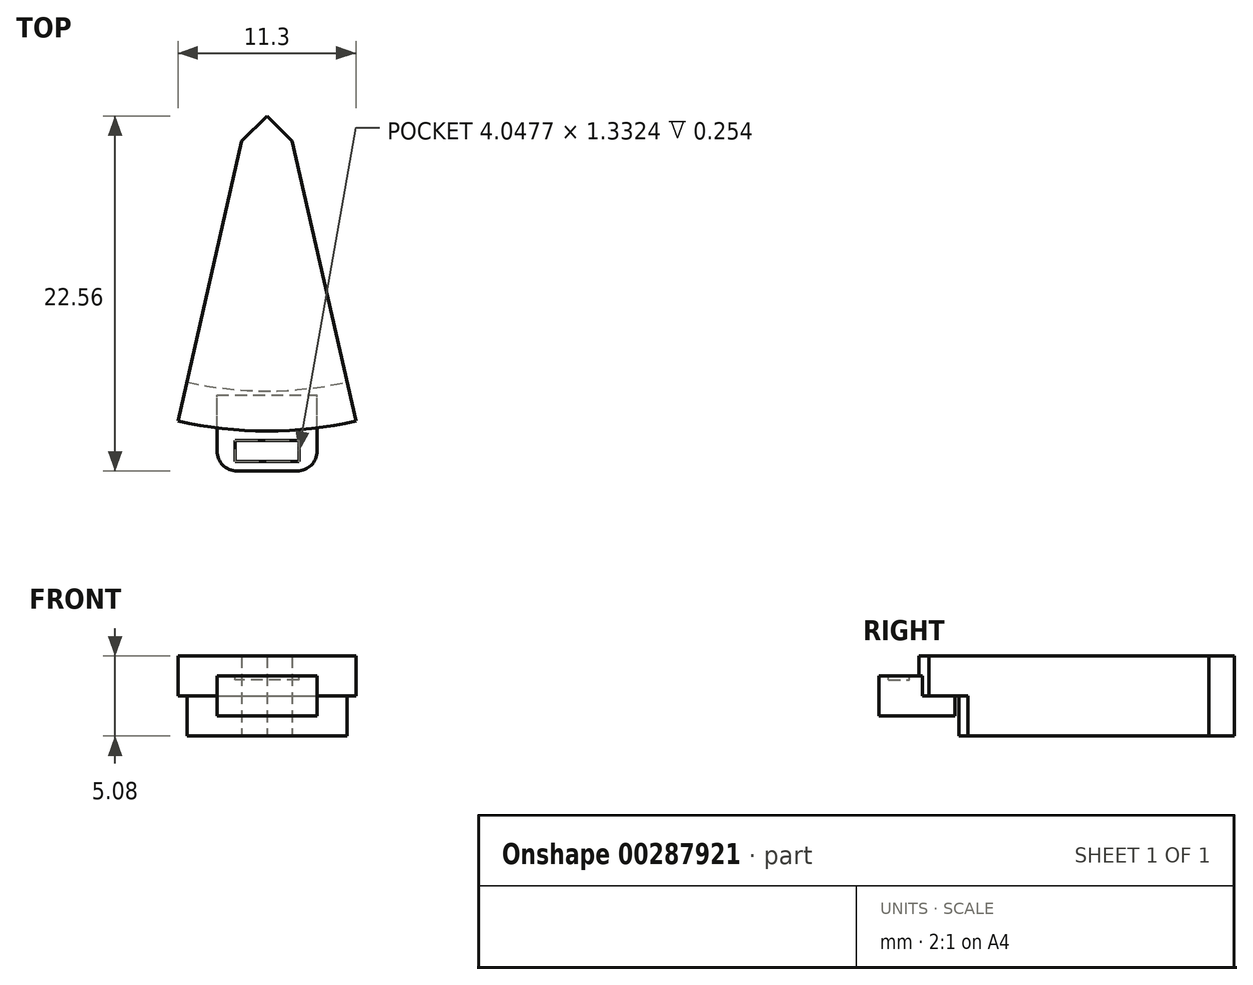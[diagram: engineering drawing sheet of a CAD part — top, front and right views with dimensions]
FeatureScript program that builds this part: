
annotation { "Feature Type Name" : "Feature", "Feature Type Description" : "" }
export const myFeature = defineFeature(function(context is Context, id is Id, definition is map)
    precondition{}
    {
        {
            var Q0;
            Q0=qCreatedBy(makeId("Top.planeOp"),FACE);
            var sketch = newSketch(context, id + "F0", { "sketchPlane" : qUnion([Q0])});
            skCircle(sketch, "E0", {"center": v(-63.88, 18.53) * mm, "radius": 25.4 * mm, "construction": true});
            skCircle(sketch, "E1", {"center": v(-63.88, 18.53) * mm, "radius": 22.86 * mm, "construction": true});
            skPoint(sketch, "E2", {"position": v(-63.88, 13.14) * mm});
            skLineSegment(sketch, "E3", {"start": v(-63.88, 62.77) * mm, "end": v(-63.88, -45.63) * mm, "construction": true});
            skLineSegment(sketch, "E4", {"start": v(-122.69, 18.53) * mm, "end": v(-1.38, 18.53) * mm, "construction": true});
            skLineSegment(sketch, "E5", {"start": v(-63.88, 13.14) * mm, "end": v(-62.28, 11.54) * mm});
            skLineSegment(sketch, "E6", {"start": v(-62.28, 11.54) * mm, "end": v(-58.23, -6.24) * mm});
            skLineSegment(sketch, "E7", {"start": v(-63.88, 13.14) * mm, "end": v(-65.48, 11.54) * mm});
            skLineSegment(sketch, "E8", {"start": v(-65.48, 11.54) * mm, "end": v(-69.53, -6.24) * mm});
            skArc(sketch, "E9", {"start": v(-58.23, -6.24) * mm, "mid": v(-63.88, -6.87) * mm, "end": v(-69.53, -6.24) * mm});
            skSolve(sketch);
        }
        {
            var Q0;
            Q0=makeQuery(id+"F0.imprint","IMPRINT",FACE,{"disambiguationData":[TD([[makeQuery(id+"F0.imprint","IMPRINT",EDGE,{"derivedFrom":sQuery(id+"F0.wireOp",EDGE,"E5")}),-1.0]])]});
            extrude(context, id + "F1", {"entities" : qUnion([Q0]), "depth" : 2.54 * mm, "offsetDistance" : 25.4 * mm});
        }
        {
            var Q0;
            Q0=makeQuery(id+"F1.opExtrude","CAP_FACE",FACE,{"disambiguationData":[OSD([sQuery(id+"F0.wireOp",EDGE,"E5"),sQuery(id+"F0.wireOp",EDGE,"E6"),sQuery(id+"F0.wireOp",EDGE,"E7"),sQuery(id+"F0.wireOp",EDGE,"E8"),sQuery(id+"F0.wireOp",EDGE,"E9")])],"isStart":false});
            var sketch = newSketch(context, id + "F2", { "sketchPlane" : qUnion([Q0])});
            skArc(sketch, "E10", {"start": v(-58.8, -3.76) * mm, "mid": v(-63.88, -4.33) * mm, "end": v(-68.97, -3.76) * mm});
            skSolve(sketch);
        }
        {
            var Q0;
            {var subQ0=sQuery(id+"F2.wireOp",EDGE,"E10");Q0=makeQuery(id+"F2.imprint","IMPRINT",FACE,{"disambiguationData":[TD([[makeQuery(id+"F2.imprint","IMPRINT",EDGE,{"derivedFrom":subQ0}),1.0]])]});}
            extrude(context, id + "F3", {"entities" : qUnion([Q0]), "operationType" : NewBodyOperationType.ADD, "oppositeDirection" : true, "depth" : 5.08 * mm, "offsetDistance" : 25.4 * mm});
        }
        {
            var Q0;
            Q0=qCreatedBy(makeId("Front.planeOp"),FACE);
            cPlane(context, id + "F4", {"entities" : qUnion([Q0]), "cplaneType" : CPlaneType.OFFSET, "offset" : 6.88 * mm, "width" : 152.4 * mm, "height" : 152.4 * mm});
        }
        {
            var Q0;
            Q0=qCreatedBy(id+"F4.planeOp",FACE);
            var sketch = newSketch(context, id + "F5", { "sketchPlane" : qUnion([Q0])});
            skLineSegment(sketch, "E11.bottom", {"start": v(-60.7, 1.27) * mm, "end": v(-67.05, 1.27) * mm});
            skLineSegment(sketch, "E11.top", {"start": v(-60.7, -1.27) * mm, "end": v(-67.05, -1.27) * mm});
            skLineSegment(sketch, "E11.left", {"start": v(-60.7, 1.27) * mm, "end": v(-60.7, -1.27) * mm});
            skLineSegment(sketch, "E11.right", {"start": v(-67.05, 1.27) * mm, "end": v(-67.05, -1.27) * mm});
            skPoint(sketch, "E11.middle", {"position": v(-63.88, 0) * mm});
            skLineSegment(sketch, "E12", {"start": v(-63.88, 18.78) * mm, "end": v(-63.88, -18.45) * mm, "construction": true});
            skLineSegment(sketch, "E13", {"start": v(-87.62, 0) * mm, "end": v(-38, 0) * mm, "construction": true});
            skSolve(sketch);
        }
        {
            var Q0;
            Q0=makeQuery(id+"F5.imprint","IMPRINT",FACE,{"disambiguationData":[TD([[makeQuery(id+"F5.imprint","IMPRINT",EDGE,{"derivedFrom":sQuery(id+"F5.wireOp",EDGE,"E11.bottom")}),1.0]])]});
            extrude(context, id + "F6", {"entities" : qUnion([Q0]), "operationType" : NewBodyOperationType.ADD, "depth" : 2.54 * mm, "offsetDistance" : 25.4 * mm, "hasSecondDirection" : true, "secondDirectionOppositeDirection" : true, "secondDirectionDepth" : 2.3 * mm});
        }
        {
            var Q0;
            Q0=makeQuery(id+"F6.opExtrude","SWEPT_FACE",FACE,{"disambiguationData":[OSD([sQuery(id+"F5.wireOp",EDGE,"E11.bottom")])]});
            var sketch = newSketch(context, id + "F7", { "sketchPlane" : qUnion([Q0])});
            skLineSegment(sketch, "E14.bottom", {"start": v(-61.86, -8.82) * mm, "end": v(-65.9, -8.82) * mm});
            skLineSegment(sketch, "E14.top", {"start": v(-61.86, -7.49) * mm, "end": v(-65.9, -7.49) * mm});
            skLineSegment(sketch, "E14.left", {"start": v(-61.86, -8.82) * mm, "end": v(-61.86, -7.49) * mm});
            skLineSegment(sketch, "E14.right", {"start": v(-65.9, -8.82) * mm, "end": v(-65.9, -7.49) * mm});
            skPoint(sketch, "E14.middle", {"position": v(-63.88, -8.15) * mm});
            skLineSegment(sketch, "E15", {"start": v(-63.88, -4.34) * mm, "end": v(-63.88, -12.25) * mm, "construction": true});
            skLineSegment(sketch, "E16", {"start": v(-68.9, -8.15) * mm, "end": v(-57.45, -8.15) * mm, "construction": true});
            skSolve(sketch);
        }
        {
            var Q0;
            Q0=makeQuery(id+"F7.imprint","IMPRINT",FACE,{"disambiguationData":[TD([[makeQuery(id+"F7.imprint","IMPRINT",EDGE,{"derivedFrom":sQuery(id+"F7.wireOp",EDGE,"E14.bottom")}),-1.0]])]});
            extrude(context, id + "F8", {"entities" : qUnion([Q0]), "operationType" : NewBodyOperationType.REMOVE, "oppositeDirection" : true, "depth" : 0.25 * mm, "offsetDistance" : 25.4 * mm});
        }
        {
            var Q0;
            Q0=makeQuery(id+"F6.opExtrude","CAP_EDGE",EDGE,{"disambiguationData":[OSD([sQuery(id+"F5.wireOp",EDGE,"E11.right")])],"isStart":false});
            var Q1;
            Q1=makeQuery(id+"F6.opExtrude","CAP_EDGE",EDGE,{"disambiguationData":[OSD([sQuery(id+"F5.wireOp",EDGE,"E11.left")])],"isStart":false});
            fillet(context, id + "F9", {"entities" : qUnion([Q0, Q1]), "radius" : 1.27 * mm, "tangentPropagation" : true, "allowEdgeOverflow" : false});
        }
    });
